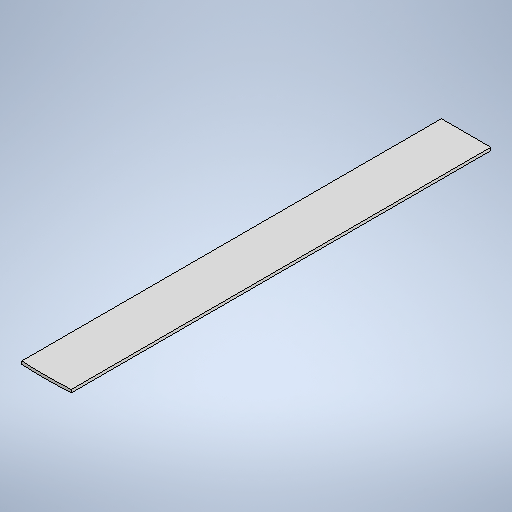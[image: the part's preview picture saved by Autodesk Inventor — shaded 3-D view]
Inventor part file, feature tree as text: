
AUTODESK INVENTOR PART (.ipt)
format: ipt  version: 2025 (Build 290162010, 162A)  size: 254,464 bytes
history: native  units: mm
features: sheet_metal_op x1, sketch x1, other x1
ambient origin geometry x8: Origin, YZ Plane, XZ Plane, XY Plane, X Axis, Y Axis, Z Axis, Center Point
bodies: Body1 (feature_tree)
feature tree (3):
  sheet_metal_op  "Face2"
  sketch  "Sketch1"  dims[d11=1100.0mm d12=900.0mm d13=25.0mm d14=25.0mm d15=3.0mm d16=25.0mm]
  other  "Plate2"
